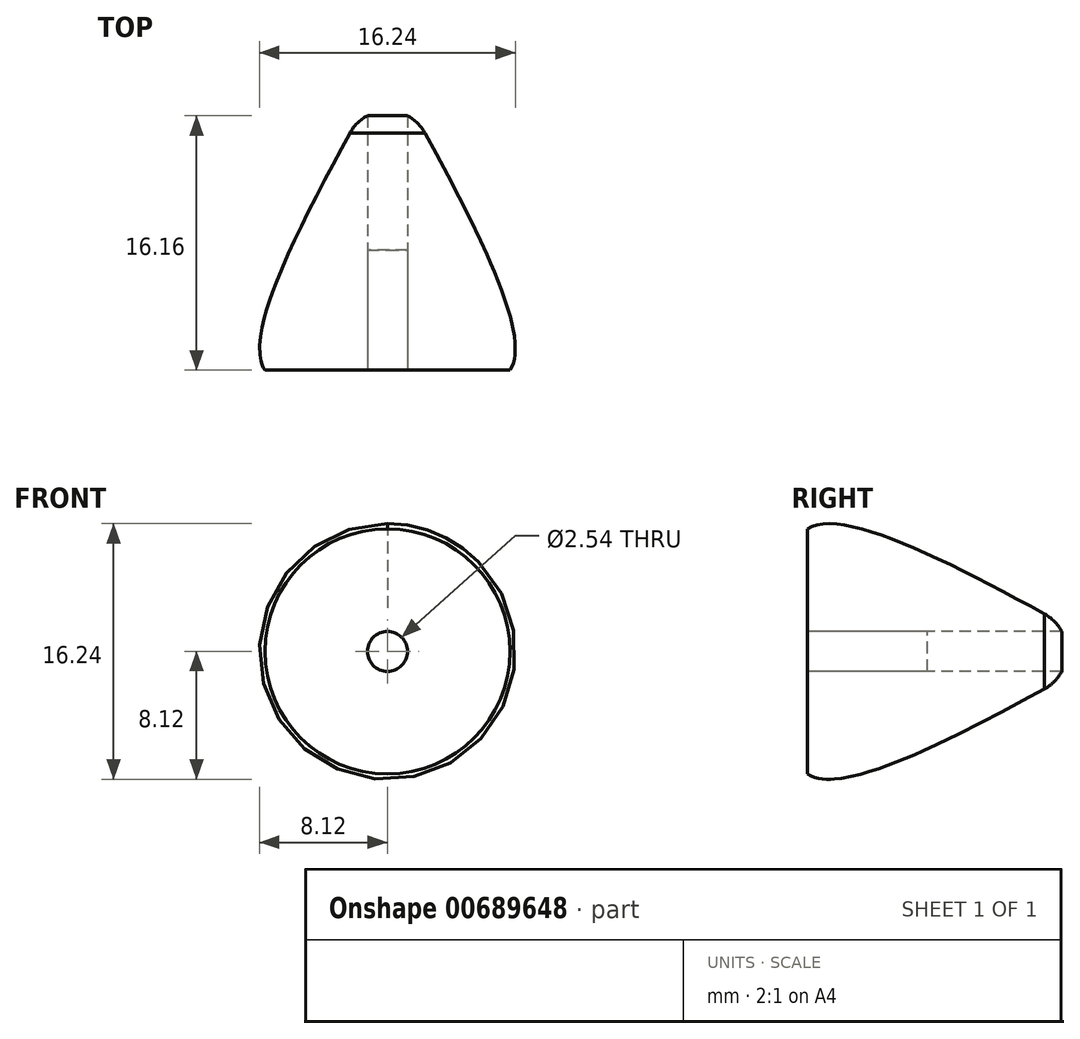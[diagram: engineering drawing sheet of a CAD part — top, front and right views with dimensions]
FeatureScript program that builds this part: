
annotation { "Feature Type Name" : "Feature", "Feature Type Description" : "" }
export const myFeature = defineFeature(function(context is Context, id is Id, definition is map)
    precondition{}
    {
        {
            var Q0;
            Q0=qCreatedBy(makeId("Top.planeOp"),FACE);
            var sketch = newSketch(context, id + "F0", { "sketchPlane" : qUnion([Q0])});
            skLineSegment(sketch, "E0", {"start": v(0, 16.47) * mm, "end": v(0, 0) * mm});
            skFitSpline(sketch, "E1.MirrorCS", {"points": [v(0, 0) * mm, v(-7.78, 0) * mm, v(0, 19.36) * mm], "startDerivative": vector(-26.8, -5.91) * mm, "endDerivative": vector(22.8, 40.87) * mm});
            skLineSegment(sketch, "E2", {"start": v(-7.78, 0) * mm, "end": v(0, 0) * mm});
            skArc(sketch, "E3", {"start": v(0, 16.47) * mm, "mid": v(-1.39, 16.09) * mm, "end": v(-2.39, 15.05) * mm});
            skPoint(sketch, "E4.end.orphan", {"position": v(7.78, 0) * mm});
            skSolve(sketch);
        }
        {
            var Q0;
            Q0=makeQuery(id+"F0.imprint","IMPRINT",FACE,{"disambiguationData":[TD([[makeQuery(id+"F0.imprint","IMPRINT",EDGE,{"derivedFrom":sQuery(id+"F0.wireOp",EDGE,"E0")}),-1.0]])]});
            var Q1;
            Q1=sQuery(id+"F0.wireOp",EDGE,"E0");
            revolve(context, id + "F1", {"entities" : qUnion([Q0]), "axis" : qUnion([Q1]), "revolveType" : RevolveType.FULL});
        }
        {
            var Q0;
            Q0=qCreatedBy(makeId("Front.planeOp"),FACE);
            var sketch = newSketch(context, id + "F2", { "sketchPlane" : qUnion([Q0])});
            skCircle(sketch, "E5", {"center": v(0, 0) * mm, "radius": 1.27 * mm});
            skSolve(sketch);
        }
        {
            var Q0;
            Q0=makeQuery(id+"F2.imprint","IMPRINT",FACE,{"disambiguationData":[TD([[makeQuery(id+"F2.imprint","IMPRINT",EDGE,{"derivedFrom":sQuery(id+"F2.wireOp",EDGE,"E5")}),1.0]])]});
            extrude(context, id + "F3", {"entities" : qUnion([Q0]), "operationType" : NewBodyOperationType.REMOVE, "oppositeDirection" : true, "depth" : 16.5 * mm, "offsetDistance" : 25.4 * mm});
        }
        {
            var Q0;
            Q0=makeQuery(id+"F1.opRevolve","SWEPT_FACE",FACE,{"disambiguationData":[OSD([sQuery(id+"F0.wireOp",EDGE,"E2")])]});
            var sketch = newSketch(context, id + "F4", { "sketchPlane" : qUnion([Q0])});
            skCircle(sketch, "E6", {"center": v(0, 0) * mm, "radius": 1.27 * mm});
            skSolve(sketch);
        }
        {
            var Q0;
            Q0=makeQuery(id+"F4.imprint","IMPRINT",FACE,{"disambiguationData":[TD([[makeQuery(id+"F4.imprint","IMPRINT",EDGE,{"derivedFrom":sQuery(id+"F4.wireOp",EDGE,"E6")}),1.0]])]});
            extrude(context, id + "F5", {"entities" : qUnion([Q0]), "depth" : -7.62 * mm, "offsetDistance" : 25.4 * mm});
        }
    });
